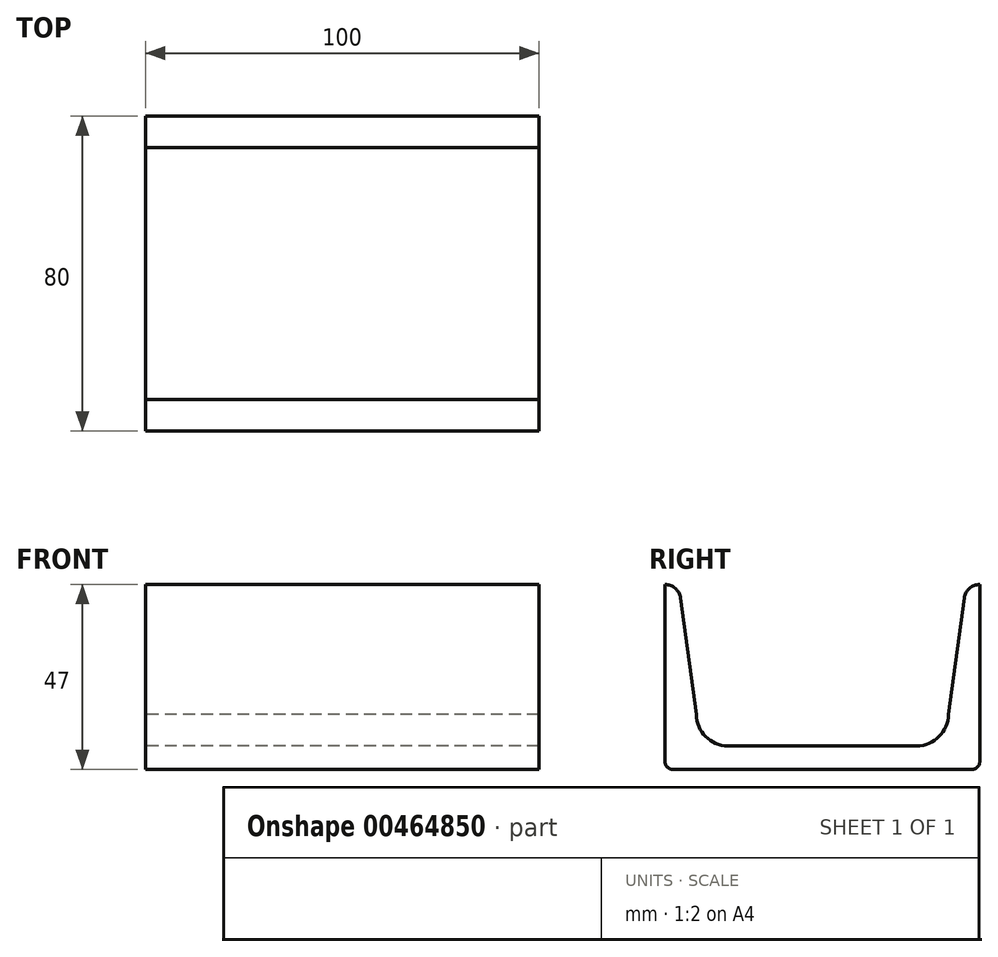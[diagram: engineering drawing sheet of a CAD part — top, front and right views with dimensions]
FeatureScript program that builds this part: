
annotation { "Feature Type Name" : "Feature", "Feature Type Description" : "" }
export const myFeature = defineFeature(function(context is Context, id is Id, definition is map)
    precondition{}
    {
        {
            var Q0;
            Q0=qCreatedBy(makeId("Right.planeOp"),FACE);
            var sketch = newSketch(context, id + "F0", { "sketchPlane" : qUnion([Q0])});
            skLineSegment(sketch, "E0.top", {"start": v(-38, -22.5) * mm, "end": v(38, -22.5) * mm});
            skLineSegment(sketch, "E0.left", {"start": v(-40, 24.5) * mm, "end": v(-40, 20.5) * mm});
            skLineSegment(sketch, "E0.right", {"start": v(40, 24.5) * mm, "end": v(40, -20.5) * mm});
            skLineSegment(sketch, "E1.top", {"start": v(-24, -16.5) * mm, "end": v(24, -16.5) * mm});
            skPoint(sketch, "E2.visualSharp", {"position": v(-32, -16.5) * mm});
            skArc(sketch, "E2.filletArc", {"start": v(-32, -8.5) * mm, "mid": v(-29.66, -14.16) * mm, "end": v(-24, -16.5) * mm});
            skPoint(sketch, "E3.visualSharp", {"position": v(-40, -22.5) * mm});
            skArc(sketch, "E3.filletArc", {"start": v(-40, -20.5) * mm, "mid": v(-39.41, -21.91) * mm, "end": v(-38, -22.5) * mm});
            skPoint(sketch, "E4.visualSharp", {"position": v(40, -22.5) * mm});
            skArc(sketch, "E4.filletArc", {"start": v(38, -22.5) * mm, "mid": v(39.41, -21.91) * mm, "end": v(40, -20.5) * mm});
            skPoint(sketch, "E5.visualSharp", {"position": v(32, -16.5) * mm});
            skArc(sketch, "E5.filletArc", {"start": v(24, -16.5) * mm, "mid": v(29.66, -14.16) * mm, "end": v(32, -8.5) * mm});
            skLineSegment(sketch, "E6", {"start": v(-32, -8.5) * mm, "end": v(-36.04, 21.04) * mm});
            skArc(sketch, "E7", {"start": v(-36.04, 21.04) * mm, "mid": v(-37.37, 23.51) * mm, "end": v(-40, 24.5) * mm});
            skPoint(sketch, "E8", {"position": v(40, 20.5) * mm});
            skArc(sketch, "E9", {"start": v(40, 24.5) * mm, "mid": v(37.37, 23.51) * mm, "end": v(36.04, 21.04) * mm});
            skLineSegment(sketch, "E10", {"start": v(32, -8.5) * mm, "end": v(36.04, 21.04) * mm});
            skLineSegment(sketch, "E11.trimOffspring", {"start": v(-40, 16.5) * mm, "end": v(-40, -20.5) * mm});
            skLineSegment(sketch, "E12", {"start": v(-40, 24.5) * mm, "end": v(-40, 16.5) * mm});
            skSolve(sketch);
        }
        {
            var Q0;
            Q0=makeQuery(id+"F0.imprint","IMPRINT",FACE,{"disambiguationData":[TD([[makeQuery(id+"F0.imprint","IMPRINT",EDGE,{"derivedFrom":sQuery(id+"F0.wireOp",EDGE,"E0.top")}),1.0]])]});
            extrude(context, id + "F1", {"entities" : qUnion([Q0]), "depth" : 100 * mm});
        }
    });
